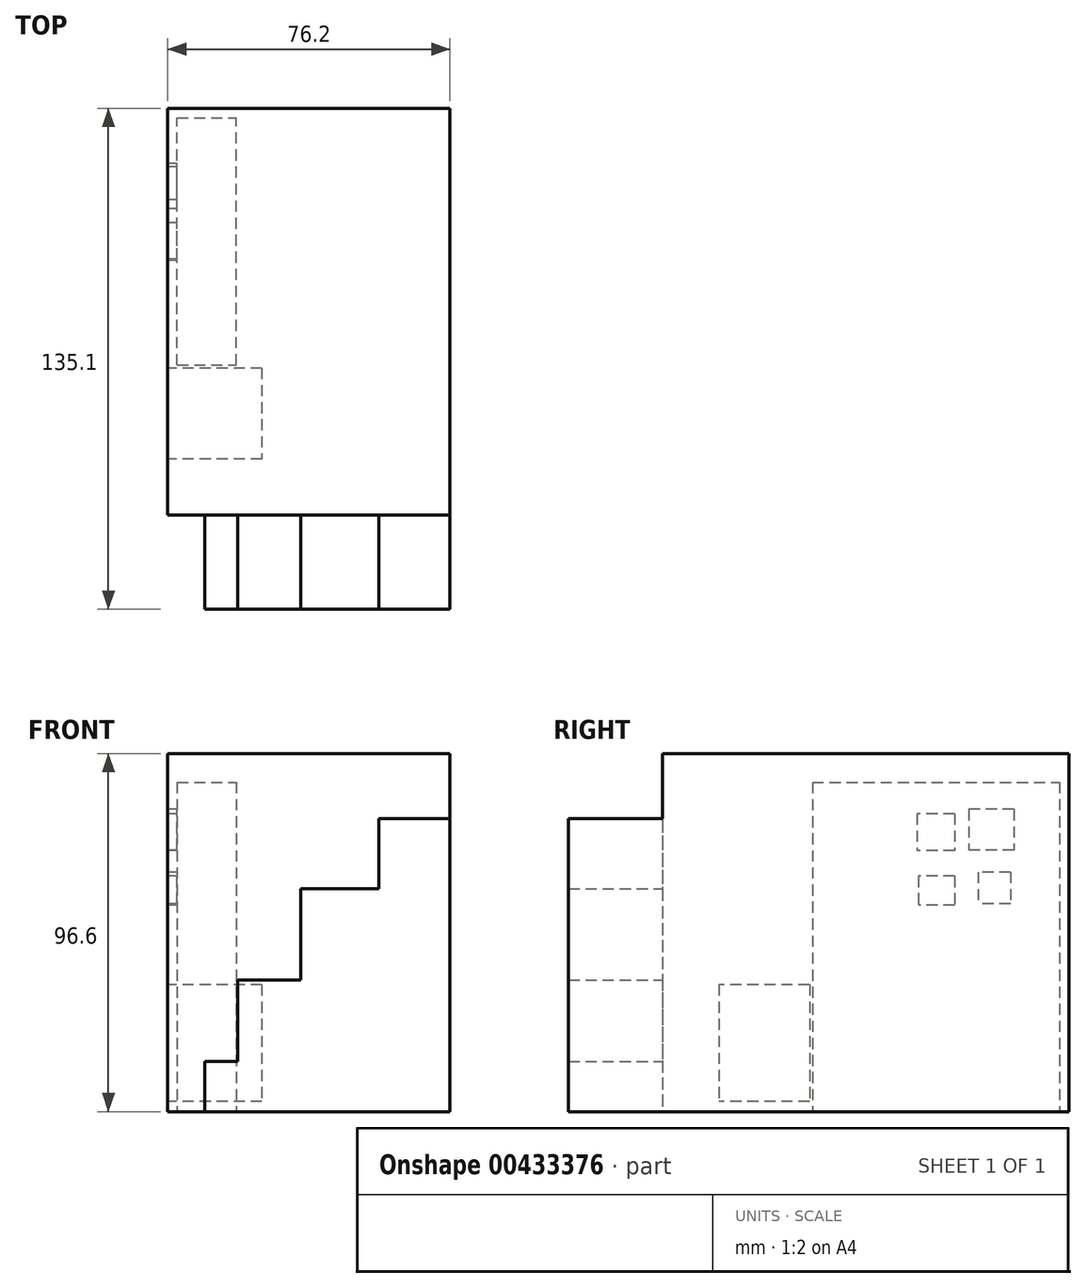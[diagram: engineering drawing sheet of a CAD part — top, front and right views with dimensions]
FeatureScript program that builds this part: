
annotation { "Feature Type Name" : "Feature", "Feature Type Description" : "" }
export const myFeature = defineFeature(function(context is Context, id is Id, definition is map)
    precondition{}
    {
        {
            var Q0;
            Q0=qCreatedBy(makeId("Right.planeOp"),FACE);
            var sketch = newSketch(context, id + "F0", { "sketchPlane" : qUnion([Q0])});
            skLineSegment(sketch, "E0.bottom", {"start": v(-55.68, 36.5) * mm, "end": v(54.02, 36.5) * mm});
            skLineSegment(sketch, "E0.top", {"start": v(-55.68, -60.1) * mm, "end": v(54.02, -60.1) * mm});
            skLineSegment(sketch, "E0.left", {"start": v(-55.68, 36.5) * mm, "end": v(-55.68, -60.1) * mm});
            skLineSegment(sketch, "E0.right", {"start": v(54.02, 36.5) * mm, "end": v(54.02, -60.1) * mm});
            skSolve(sketch);
        }
        {
            var Q0;
            Q0 = qSketchRegion(id + "F0", true);
            extrude(context, id + "F1", {"entities" : qUnion([Q0]), "depth" : 76.2 * mm});
        }
        {
            var Q0;
            Q0=makeQuery(id+"F1.opExtrude","SWEPT_FACE",FACE,{"disambiguationData":[OSD([sQuery(id+"F0.wireOp",EDGE,"E0.left")])]});
            var sketch = newSketch(context, id + "F2", { "sketchPlane" : qUnion([Q0])});
            skLineSegment(sketch, "E1", {"start": v(76.2, 18.94) * mm, "end": v(57.02, 18.94) * mm});
            skLineSegment(sketch, "E2", {"start": v(57.02, 18.94) * mm, "end": v(57.02, 0) * mm});
            skLineSegment(sketch, "E3", {"start": v(57.02, 0) * mm, "end": v(35.86, 0) * mm});
            skLineSegment(sketch, "E4", {"start": v(35.86, 0) * mm, "end": v(35.86, -24.55) * mm});
            skLineSegment(sketch, "E5", {"start": v(35.86, -24.55) * mm, "end": v(18.92, -24.55) * mm});
            skLineSegment(sketch, "E6", {"start": v(18.92, -24.55) * mm, "end": v(18.92, -46.6) * mm});
            skLineSegment(sketch, "E7", {"start": v(18.92, -46.6) * mm, "end": v(9.97, -46.6) * mm});
            skLineSegment(sketch, "E8", {"start": v(9.97, -46.6) * mm, "end": v(9.97, -60.1) * mm});
            skSolve(sketch);
        }
        {
            var Q0;
            {var subQ4=sQuery(id+"F2.wireOp",EDGE,"E1");Q0=makeQuery(id+"F2.imprint","IMPRINT",FACE,{"disambiguationData":[TD([[makeQuery(id+"F2.imprint","IMPRINT",EDGE,{"derivedFrom":subQ4}),1.0]])]});}
            extrude(context, id + "F3", {"entities" : qUnion([Q0]), "operationType" : NewBodyOperationType.ADD, "depth" : 25.4 * mm});
        }
        {
            var Q0;
            Q0=makeQuery(id+"F1.opExtrude","CAP_FACE",FACE,{"disambiguationData":[OSD([sQuery(id+"F0.wireOp",EDGE,"E0.bottom"),sQuery(id+"F0.wireOp",EDGE,"E0.top"),sQuery(id+"F0.wireOp",EDGE,"E0.left"),sQuery(id+"F0.wireOp",EDGE,"E0.right")])],"isStart":true});
            var sketch = newSketch(context, id + "F4", { "sketchPlane" : qUnion([Q0])});
            skLineSegment(sketch, "E9.bottom", {"start": v(-43.05, 25.47) * mm, "end": v(-8.92, 25.47) * mm});
            skLineSegment(sketch, "E9.top", {"start": v(-43.05, -7.73) * mm, "end": v(-8.92, -7.73) * mm});
            skLineSegment(sketch, "E9.left", {"start": v(-43.05, 25.47) * mm, "end": v(-43.05, -7.73) * mm});
            skLineSegment(sketch, "E9.right", {"start": v(-8.92, 25.47) * mm, "end": v(-8.92, -7.73) * mm});
            skLineSegment(sketch, "E10.bottom", {"start": v(-39.16, 21.46) * mm, "end": v(-26.99, 21.46) * mm});
            skLineSegment(sketch, "E10.top", {"start": v(-39.16, 10.48) * mm, "end": v(-26.99, 10.48) * mm});
            skLineSegment(sketch, "E10.left", {"start": v(-39.16, 21.46) * mm, "end": v(-39.16, 10.48) * mm});
            skLineSegment(sketch, "E10.right", {"start": v(-26.99, 21.46) * mm, "end": v(-26.99, 10.48) * mm});
            skLineSegment(sketch, "E11.bottom", {"start": v(-23.12, 20.3) * mm, "end": v(-12.97, 20.3) * mm});
            skLineSegment(sketch, "E11.top", {"start": v(-23.12, 10.34) * mm, "end": v(-12.97, 10.34) * mm});
            skLineSegment(sketch, "E11.left", {"start": v(-23.12, 20.3) * mm, "end": v(-23.12, 10.34) * mm});
            skLineSegment(sketch, "E11.right", {"start": v(-12.97, 20.3) * mm, "end": v(-12.97, 10.34) * mm});
            skLineSegment(sketch, "E12.bottom", {"start": v(-38.24, 4.56) * mm, "end": v(-29.44, 4.56) * mm});
            skLineSegment(sketch, "E12.top", {"start": v(-38.24, -3.98) * mm, "end": v(-29.44, -3.98) * mm});
            skLineSegment(sketch, "E12.left", {"start": v(-38.24, 4.56) * mm, "end": v(-38.24, -3.98) * mm});
            skLineSegment(sketch, "E12.right", {"start": v(-29.44, 4.56) * mm, "end": v(-29.44, -3.98) * mm});
            skLineSegment(sketch, "E13.bottom", {"start": v(-23.15, 3.48) * mm, "end": v(-13.38, 3.48) * mm});
            skLineSegment(sketch, "E13.top", {"start": v(-23.15, -4.35) * mm, "end": v(-13.38, -4.35) * mm});
            skLineSegment(sketch, "E13.left", {"start": v(-23.15, 3.48) * mm, "end": v(-23.15, -4.35) * mm});
            skLineSegment(sketch, "E13.right", {"start": v(-13.38, 3.48) * mm, "end": v(-13.38, -4.35) * mm});
            skSolve(sketch);
        }
        {
            var Q0;
            Q0=makeQuery(id+"F4.imprint","IMPRINT",FACE,{"disambiguationData":[TD([[makeQuery(id+"F4.imprint","IMPRINT",EDGE,{"derivedFrom":sQuery(id+"F4.wireOp",EDGE,"E10.bottom")}),-1.0]])]});
            var Q1;
            Q1=makeQuery(id+"F4.imprint","IMPRINT",FACE,{"disambiguationData":[TD([[makeQuery(id+"F4.imprint","IMPRINT",EDGE,{"derivedFrom":sQuery(id+"F4.wireOp",EDGE,"E12.bottom")}),-1.0]])]});
            var Q2;
            Q2=makeQuery(id+"F4.imprint","IMPRINT",FACE,{"disambiguationData":[TD([[makeQuery(id+"F4.imprint","IMPRINT",EDGE,{"derivedFrom":sQuery(id+"F4.wireOp",EDGE,"E13.bottom")}),-1.0]])]});
            var Q3;
            Q3=makeQuery(id+"F4.imprint","IMPRINT",FACE,{"disambiguationData":[TD([[makeQuery(id+"F4.imprint","IMPRINT",EDGE,{"derivedFrom":sQuery(id+"F4.wireOp",EDGE,"E11.bottom")}),-1.0]])]});
            extrude(context, id + "F5", {"entities" : qUnion([Q0, Q1, Q2, Q3]), "operationType" : NewBodyOperationType.REMOVE, "oppositeDirection" : true, "depth" : 12.7 * mm});
        }
        {
            var Q0;
            Q0=makeQuery(id+"F1.opExtrude","CAP_FACE",FACE,{"disambiguationData":[OSD([sQuery(id+"F0.wireOp",EDGE,"E0.bottom"),sQuery(id+"F0.wireOp",EDGE,"E0.top"),sQuery(id+"F0.wireOp",EDGE,"E0.left"),sQuery(id+"F0.wireOp",EDGE,"E0.right")])],"isStart":true});
            var sketch = newSketch(context, id + "F6", { "sketchPlane" : qUnion([Q0])});
            skLineSegment(sketch, "E14.bottom", {"start": v(13, -22.7) * mm, "end": v(43.92, -22.7) * mm});
            skLineSegment(sketch, "E14.top", {"start": v(13, -60.1) * mm, "end": v(43.92, -60.1) * mm});
            skLineSegment(sketch, "E14.left", {"start": v(13, -22.7) * mm, "end": v(13, -60.1) * mm});
            skLineSegment(sketch, "E14.right", {"start": v(43.92, -22.7) * mm, "end": v(43.92, -60.1) * mm});
            skSolve(sketch);
        }
        {
            var Q0;
            Q0=makeQuery(id+"F6.imprint","IMPRINT",FACE,{"disambiguationData":[TD([[makeQuery(id+"F6.imprint","IMPRINT",EDGE,{"derivedFrom":sQuery(id+"F6.wireOp",EDGE,"E14.bottom")}),-1.0]])]});
            var sketch = newSketch(context, id + "F7", { "sketchPlane" : qUnion([Q0])});
            skLineSegment(sketch, "E15.bottom", {"start": v(16.02, -25.84) * mm, "end": v(40.53, -25.84) * mm});
            skLineSegment(sketch, "E15.top", {"start": v(16.02, -57.32) * mm, "end": v(40.53, -57.32) * mm});
            skLineSegment(sketch, "E15.left", {"start": v(16.02, -25.84) * mm, "end": v(16.02, -57.32) * mm});
            skLineSegment(sketch, "E15.right", {"start": v(40.53, -25.84) * mm, "end": v(40.53, -57.32) * mm});
            skSolve(sketch);
        }
        {
            var Q0;
            Q0=makeQuery(id+"F7.imprint","IMPRINT",FACE,{"disambiguationData":[TD([[makeQuery(id+"F7.imprint","IMPRINT",EDGE,{"derivedFrom":sQuery(id+"F7.wireOp",EDGE,"E15.bottom")}),-1.0]])]});
            extrude(context, id + "F8", {"entities" : qUnion([Q0]), "operationType" : NewBodyOperationType.REMOVE, "oppositeDirection" : true, "depth" : 25.4 * mm});
        }
        {
            var Q0;
            {var subQ0=sQuery(id+"F0.wireOp",EDGE,"E0.top");Q0=makeQuery(id+"F3.boolean.opBoolean","MERGE",FACE,{"derivedFrom":[makeQuery(id+"F1.opExtrude","SWEPT_FACE",FACE,{"disambiguationData":[OSD([subQ0])]}),makeQuery(id+"F3.opExtrude","SWEPT_FACE",FACE,{"disambiguationData":[OSD([subQ0,sQuery(id+"F0.wireOp",EDGE,"E0.left")])]})]});}
            var sketch = newSketch(context, id + "F9", { "sketchPlane" : qUnion([Q0])});
            skLineSegment(sketch, "E16.bottom", {"start": v(2.54, 15.23) * mm, "end": v(18.44, 15.23) * mm});
            skLineSegment(sketch, "E16.top", {"start": v(2.54, -51.48) * mm, "end": v(18.44, -51.48) * mm});
            skLineSegment(sketch, "E16.left", {"start": v(2.54, 15.23) * mm, "end": v(2.54, -51.48) * mm});
            skLineSegment(sketch, "E16.right", {"start": v(18.44, 15.23) * mm, "end": v(18.44, -51.48) * mm});
            skSolve(sketch);
        }
        {
            var Q0;
            Q0=makeQuery(id+"F9.imprint","IMPRINT",FACE,{"disambiguationData":[TD([[makeQuery(id+"F9.imprint","IMPRINT",EDGE,{"derivedFrom":sQuery(id+"F9.wireOp",EDGE,"E16.bottom")}),-1.0]])]});
            extrude(context, id + "F10", {"entities" : qUnion([Q0]), "operationType" : NewBodyOperationType.REMOVE, "oppositeDirection" : true, "depth" : 88.9 * mm});
        }
    });
